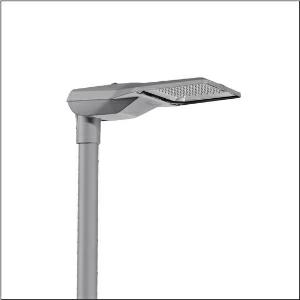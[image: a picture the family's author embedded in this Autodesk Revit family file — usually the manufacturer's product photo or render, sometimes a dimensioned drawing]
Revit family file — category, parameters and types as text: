
# Revit family: streetlight_sl_21_midi___st0_8a_5xe3c33s08mb_531e
name_source: partatom
category: Lighting Fixtures
units: mm (PartAtom-declared; Revit-internal decimal feet)

## family parameters
Cut with Voids When Loaded = No
Host = Face
Light Source = No
Part Type = Normal
Room Calculation Point = No
Round Connector Dimension = Use Diameter
Shared = No

## types (1)
- --- (1 x LED, 18270 lm, 136 W, 3000K)
    Apparent Load = 136 VA
    CIE Flux Codes = 38 75 97 100 100
    Color Rendering = 70
    Color Temperature = 3000K
    Default Elevation = 1800 mm
    Description = Streetlight SL 21 midi, mast luminaire, primary light control with lens, of PMMA, primary optical cover: cover, of toughened safety glass, transparent, light distribution: ST0.8a, light emission: direct distribution, primary light characteristic: asymmetric, installation type: side-entry, post-top, LED, High Power LED, rated luminous flux: 18.270lm, luminous efficacy: 134lm/W, light colour: 730, colour temperature: 3000K, control: overheat protection, constant luminous flux control, time-dependent luminous flux control, flexible luminous flux parameterisation, presetting dimming logarithmic, mains connection: 230..240V, AC, 50/60Hz, start of lifetime: 136W, end of service life: 142W, reduction: 61W, luminaire housing, of diecast aluminium, powder-coated, Siteco® metallic grey (DB 702S), corrosivity category C5 mid according to DIN EN ISO 12944, please order mast flange separately, inclination adjustable: 0°, 5°, 10°, 15°, sealing non-destructively replaceable, multi-level sealing system, length: 644mm, width: 335mm, height: 110mm, mast flange for spigot size: 42mm (side-entry): 5XC10008XM4, 60/48mm (side-entry/post-top): 5XC10108XM2, 76/60mm (side-entry/post-top): 5XC10108XM1, Smart Interface above, protection rating (complete): IP66, insulation class (complete): insulation class II (safety insulation), certification: CE, ENEC, ENEC+, VDE, impact resistance: IK09, permissible operating ambient temperature for outdoor applications: -40..+50°C, standard-compliant lighting for roads and squares, packaging unit: 1 piece

Light Distribution: ST0.8a
    Height = 111 mm
    Lamp = 1 x LED
    Lamp Light Flux = 18270 lm
    Lamp Power = 136 W
    Lamp count = 1
    Length = 644 mm
    Luminous efficacy = 134 lm/W
    Manufacturer = Siteco
    ModVariant = No
    Model = 5XE3C33S08MB
    Number of Poles = 1
    OnlyDefault = Yes
    Power Factor = 1
    Product Name = Streetlight SL 21 midi | ST0.8a
    Product group = mast luminaire | pylon top
    ProductGroupID = 6100
    Protection Class = Protection class II
    Protection Degree = IP 66
    RLX_Detail_Level = 1
    RLX_Emergency_Light_Flux = 0 lm
    RLX_Emergency_Type = 0
    RLX_Emergency_Type_DB = No
    RlxData = <blob elided: 90681 chars, md5=657660ab>
    Socket = socket
    Standby Power = 0 W
    System Light Flux = 18270 lm
    System Power = 136 W
    Type Comments = factory setting: luminous flux: 100 % | dim-lin: 254 | 695 mA
    Type Image = l_1004302.jpg
    URL = http://relux.com
    VarID = @adj_137859
    Voltage = 0 V
    Weight = 0.00 kg
    Width = 336 mm

## geometry (parser evidence)
native form markers: Blend x4, Sweep x12
no freeform markers — native parametric forms only
